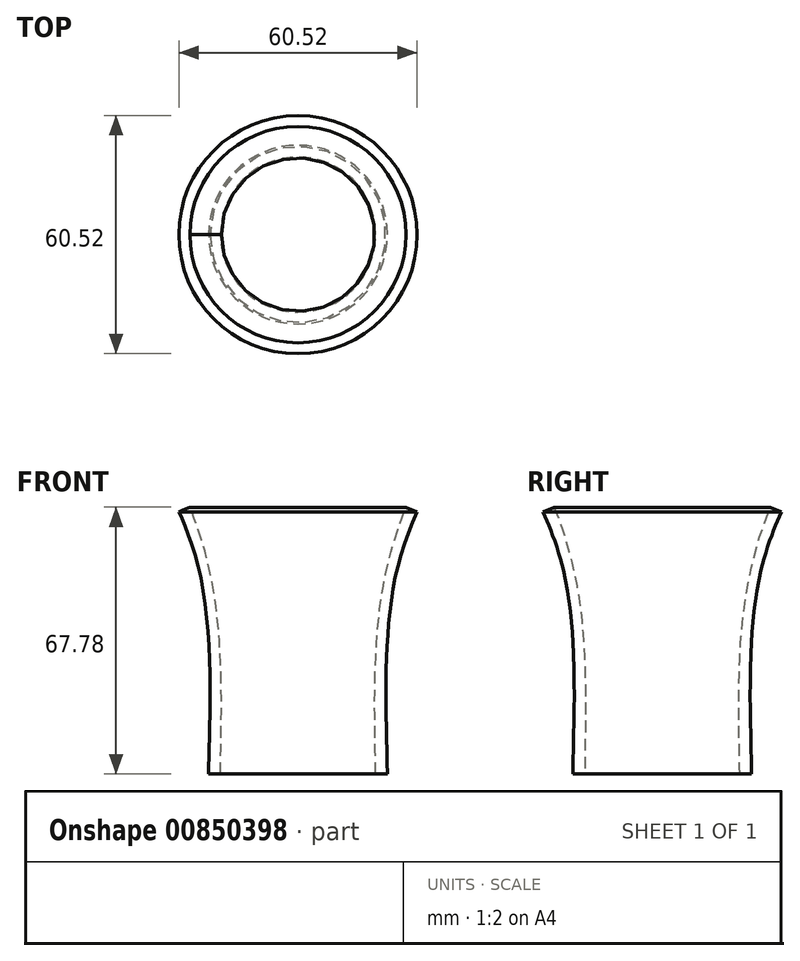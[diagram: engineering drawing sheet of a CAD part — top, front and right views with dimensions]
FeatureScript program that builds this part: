
annotation { "Feature Type Name" : "Feature", "Feature Type Description" : "" }
export const myFeature = defineFeature(function(context is Context, id is Id, definition is map)
    precondition{}
    {
        {
            var Q0;
            Q0=qCreatedBy(makeId("Front.planeOp"),FACE);
            var sketch = newSketch(context, id + "F0", { "sketchPlane" : qUnion([Q0])});
            skLineSegment(sketch, "E0", {"start": v(0, 0) * mm, "end": v(0, 61.43) * mm, "construction": true});
            skFitSpline(sketch, "E1", {"points": [v(19.7, 0) * mm, v(27.49, 67.78) * mm], "startDerivative": vector(-1.26, 76.62) * mm, "endDerivative": vector(26.66, 64.43) * mm});
            skFitSpline(sketch, "E2.0", {"points": [v(22.7, 0.05) * mm, v(22.6, 6.44) * mm, v(22.35, 18.58) * mm, v(22.81, 35.33) * mm, v(24.97, 51.13) * mm, v(28.1, 61.43) * mm, v(30.26, 66.63) * mm]});
            skLineSegment(sketch, "E3", {"start": v(19.7, 0) * mm, "end": v(22.7, 0.05) * mm});
            skLineSegment(sketch, "E4", {"start": v(27.49, 67.78) * mm, "end": v(30.26, 66.63) * mm});
            skSolve(sketch);
        }
        {
            var Q0;
            Q0=makeQuery(id+"F0.imprint","IMPRINT",FACE,{"disambiguationData":[TD([[makeQuery(id+"F0.imprint","IMPRINT",EDGE,{"derivedFrom":sQuery(id+"F0.wireOp",EDGE,"E1")}),-1.0]])]});
            var Q1;
            Q1=sQuery(id+"F0.wireOp",EDGE,"E0");
            revolve(context, id + "F1", {"surfaceOperationType" : NewSurfaceOperationType.NEW, "entities" : qUnion([Q0]), "axis" : qUnion([Q1]), "revolveType" : RevolveType.FULL});
        }
    });
